# Revit family: PD9-GH-FP types Avec hôte
name_source: partatom
category: Dispositifs d'éclairage
units: mm (PartAtom-declared; Revit-internal decimal feet)

## family parameters
Conserver l'orientation des annotations = Oui
Cote de connecteur circulaire = Utiliser le diamètre
Couper avec des vides une fois chargée = Non
Hôte = Face
Partagée = Non
Point de calcul de pièce = Non
Type d'élément = Normal

## types (10) — shared parameters
Code d'assemblage = D5010200
Fabricant = B.E.G.
Hauteur de montage max = 1000 cm
Image du type = 360°.jpg
Marque = LUXOMAT
Mode de pose = Faux Plafond
URL = http://www.luxomat.com
zero-valued in all types: Elévation par défaut

## per-type parameters (varying)
| type | Alimentation | Charge Cos ɸ =0.5 | Charge Cos ɸ =1 | Charge LED | Classe | Commentaires du type | Consommation | IP | Modèle | Relais | Référence | Température ambiante | Type de Sortie |
| 01- PD9-GH-FP Générique | 110-240 V AC |  |  |  | II | MINI.DET.PRES.GRANDE HAUTEUR.360°/Ø6M FAUX PLAFOND |  | 20 | PD9-GH-FP |  |  | -25°C at +50°C |  |
| 02- PD9-1C-GH-FP réf 92934 | 110-240 V AC | 500 VA | 1000 W | 200 W | II | MINI.DET.PRES.GRANDE HAUTEUR.1 CONTACT.360°/Ø6M FAUX PLAFOND | 0,5 W | 20 | PD9-1C-GH-FP | 4,3 A | 92934 | -25°C at +50°C | TOR |
| 03- PD9-M-1C-GH-FP réf 92923 | 110-240 V AC | 1150 VA | 2300 W | 300 W | II | MINI.DET.PRES.MAITRE.GRANDE HAUTEUR.1 CONTACT.360°/Ø6M FAUX PLAFOND | 0,4 W | 20 | PD9-M-1C-GH-FP | 10 A | 92923 | -25°C at +50°C | TOR |
| 04- PD9-M-1C-IP65-GH-FP réf 92931 | 110-240 V AC | 1150 VA | 2300 W | 300 W | Alim II / Tête III | MINI.DET.PRES.MAITRE.GRANDE HAUTEUR.IP65.1 CONTACT.360°/Ø6M FAUX PLAFOND | 1 W | Alim 20 / Tête 65 | PD9-M-1C-IP65-GH-FP | 10 A | 92931 | -25°C at +50°C | TOR |
| 05- PD9-M-DALI/DSI-GH-FP réf 92938 | 110-240 V AC |  |  |  | II | MINI.DET.PRES.MAITRE.GRANDE HAUTEUR.DALI/DSI.360°/Ø6M FAUX PLAFOND | 0,45 W | 20 | PD9-M-DALI/DSI-GH-FP |  | 92938 | -25°C at +50°C | DALI (50 ballasts maxi) |
| 06- PD9-M-DIM-GH-FP réf 92924 | 110-240 V AC | 1150 VA | 2300 W | 300 W | II | MINI.DET.PRES.MAITRE.GRANDE HAUTEUR.DIM(1-10V).360°/Ø6M FAUX PLAFOND | 0,47 W | 20 | PD9-M-DIM-GH-FP | 10 A | 92924 | -25°C at +50°C | DIM (50 ballasts maxi) |
| 07- PD9-S-GH-FP réf 92928 | 110-240 V AC | 0 | 0 | 0 | II | MINI.DET.PRES.ESCLAVE.GRANDE HAUTEUR.360°/Ø6M FAUX PLAFOND | 0,25 W | 20 | PD9-S-GH-FP | 0 | 92928 | -25°C at +50°C | Esclave |
| 08- PD9-S-IP65-GH-FP réf 92933 | 110-240 V AC | 0 | 0 | 0 | Tête III | MINI.DET.PRES.ESCLAVE.GRANDE HAUTEUR.IP65.360°/Ø6M FAUX PLAFOND | 0,25 W | Tête 65 | PD9-S-IP65-GH-FP | 0 | 92933 | -25°C at +50°C | Esclave |
| 09- PD9-KNX-GH-DX-FP réf 93391 | 24 V DC par Bus KNX | 0 | 0 | 0 | II | MINI.DET.PRES.GRANDE HAUTEUR.KNX.VERSION DELUXE.360°/Ø6M FAUX PLAFOND | 12 mA | 20 | PD9-KNX-GH-DX-FP | 0 | 93391 | -5°C at +45°C | KNX - 1 sortie Eclairage TOR ou GRADATION / 3 sorties Présence / Capteur de température |
| 10- PD9-KNXs-GH-DX-FP réf 93521 | 24 V DC par Bus KNX | 0 | 0 | 0 | II | MINI.DET.PRES.GRANDE HAUTEUR.KNX Sécure.VERSION DELUXE.360°/Ø6M FAUX PLAFOND | 12 mA | 20 | PD9-KNXs-GH-DX-FP | 0 | 93521 | -5°C at +45°C | KNX Sécure - 1 sortie Eclairage TOR ou GRADATION / 3 sorties Présence |
